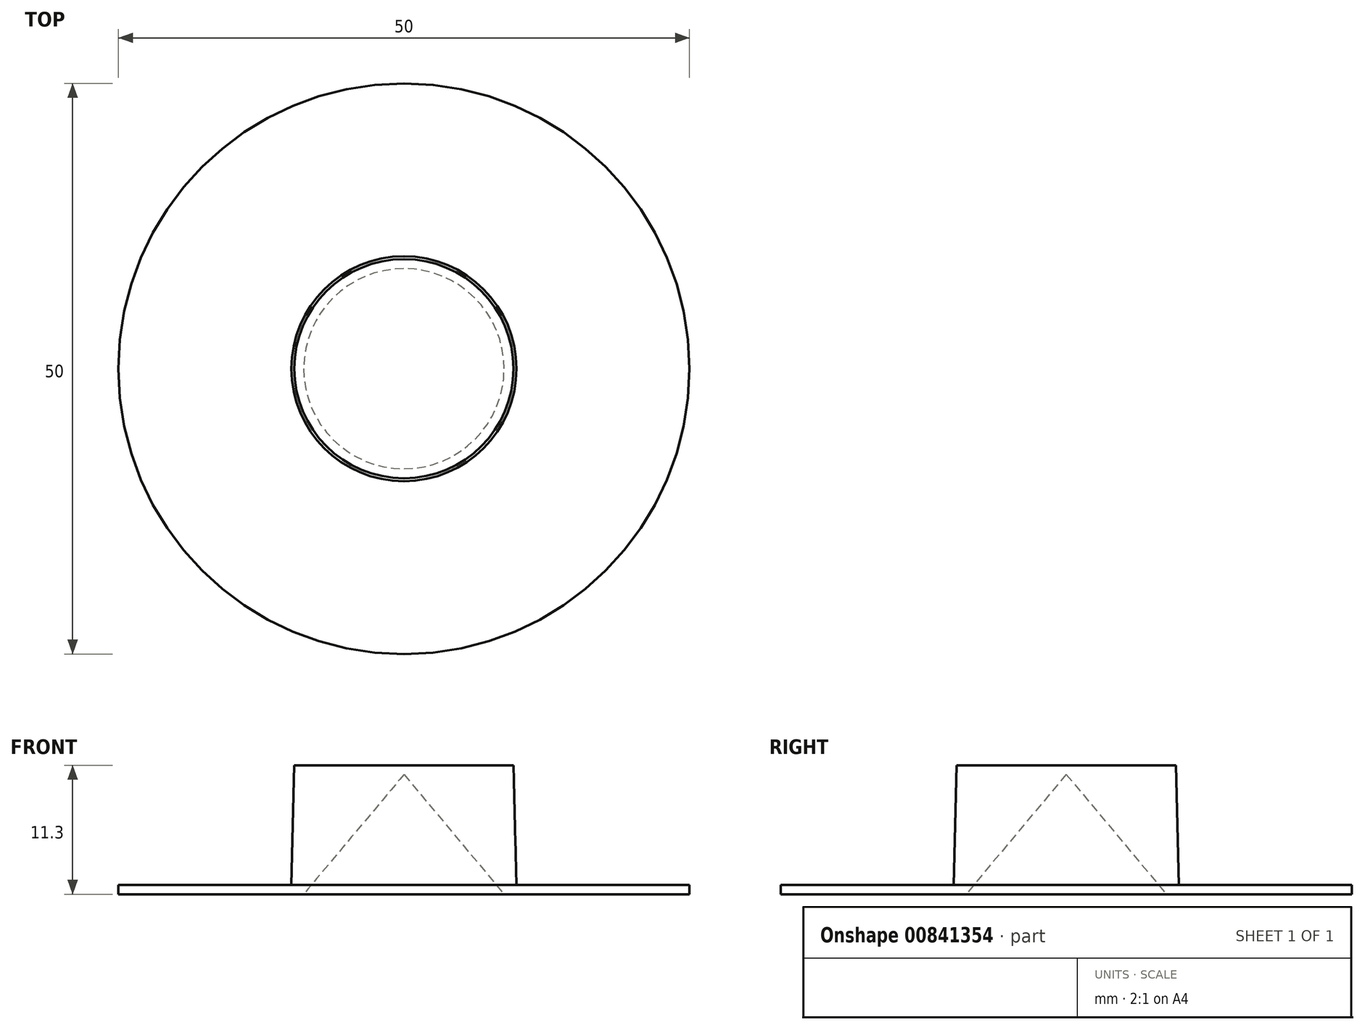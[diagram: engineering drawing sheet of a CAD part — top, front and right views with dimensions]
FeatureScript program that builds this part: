
annotation { "Feature Type Name" : "Feature", "Feature Type Description" : "" }
export const myFeature = defineFeature(function(context is Context, id is Id, definition is map)
    precondition{}
    {
        {
            var Q0;
            Q0=qCreatedBy(makeId("Front.planeOp"),FACE);
            var sketch = newSketch(context, id + "F0", { "sketchPlane" : qUnion([Q0])});
            skLineSegment(sketch, "E0", {"start": v(8.77, 0) * mm, "end": v(25, 0) * mm});
            skLineSegment(sketch, "E1", {"start": v(9.6, 11.3) * mm, "end": v(9.86, 0.8) * mm});
            skLineSegment(sketch, "E2", {"start": v(9.6, 11.3) * mm, "end": v(0, 11.3) * mm});
            skLineSegment(sketch, "E3.0", {"start": v(9.86, 0.8) * mm, "end": v(25, 0.8) * mm});
            skLineSegment(sketch, "E4", {"start": v(0, 11.3) * mm, "end": v(0, 10.5) * mm});
            skLineSegment(sketch, "E5", {"start": v(0, 10.5) * mm, "end": v(8.77, 0) * mm});
            skLineSegment(sketch, "E6", {"start": v(25, 0.8) * mm, "end": v(25, 0) * mm});
            skSolve(sketch);
        }
        {
            var Q0;
            Q0 = qSketchRegion(id + "F0", true);
            var Q1;
            Q1=sQuery(id+"F0.wireOp",EDGE,"E4");
            revolve(context, id + "F1", {"surfaceOperationType" : NewSurfaceOperationType.NEW, "entities" : qUnion([Q0]), "axis" : qUnion([Q1]), "revolveType" : RevolveType.FULL});
        }
    });
